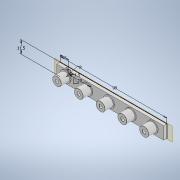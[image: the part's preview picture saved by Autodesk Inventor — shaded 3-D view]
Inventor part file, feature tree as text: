
AUTODESK INVENTOR PART (.ipt)
format: ipt  version: 2021 (Build 250183000, 183)  size: 231,936 bytes
history: native  units: mm
features: extrude x4, sketch x4, chamfer x1
ambient origin geometry x8: Origin, YZ Plane, XZ Plane, XY Plane, X Axis, Y Axis, Z Axis, Center Point
bodies: Solid1 (feature_tree)
feature tree (9):
  extrude  "Extrusion1"  Depth=8.0mm
  extrude  "Extrusion2"  Depth=8.0mm
  extrude  "Extrusion3"  Depth=10.0mm
  chamfer  "Chamfer1"  Distance=3.0mm
  extrude  "Extrusion4"  Depth=0.5mm
  sketch  "Sketch1"  dims[d0=11.5mm d1=8.0mm]
  sketch  "Sketch2"  dims[d2=8.0mm d3=1.5mm]
  sketch  "Sketch3"  dims[d4=1.0mm d5=50.0mm d7=20.0mm d8=10.0mm d10=10.0mm]
  sketch  "Sketch4"  dims[d12=98.0mm d13=3.0mm d14=0.0mm d15=0.05mm d17=0.05mm d18=0.1mm d19=0.1mm d20=0.15mm d21=0.15mm d22=0.2mm d23=0.2mm d24=8.0mm d25=0.0mm d26=1.0mm d27=50.0mm d29=20.0mm d30=10.0mm d32=10.0mm d34=0.5mm d35=0.0mm d36=0.1mm d37=2.0mm d38=45.0deg d39=15.0mm d40=5.0mm d41=5.0mm d42=0.5mm d43=0.0mm]
